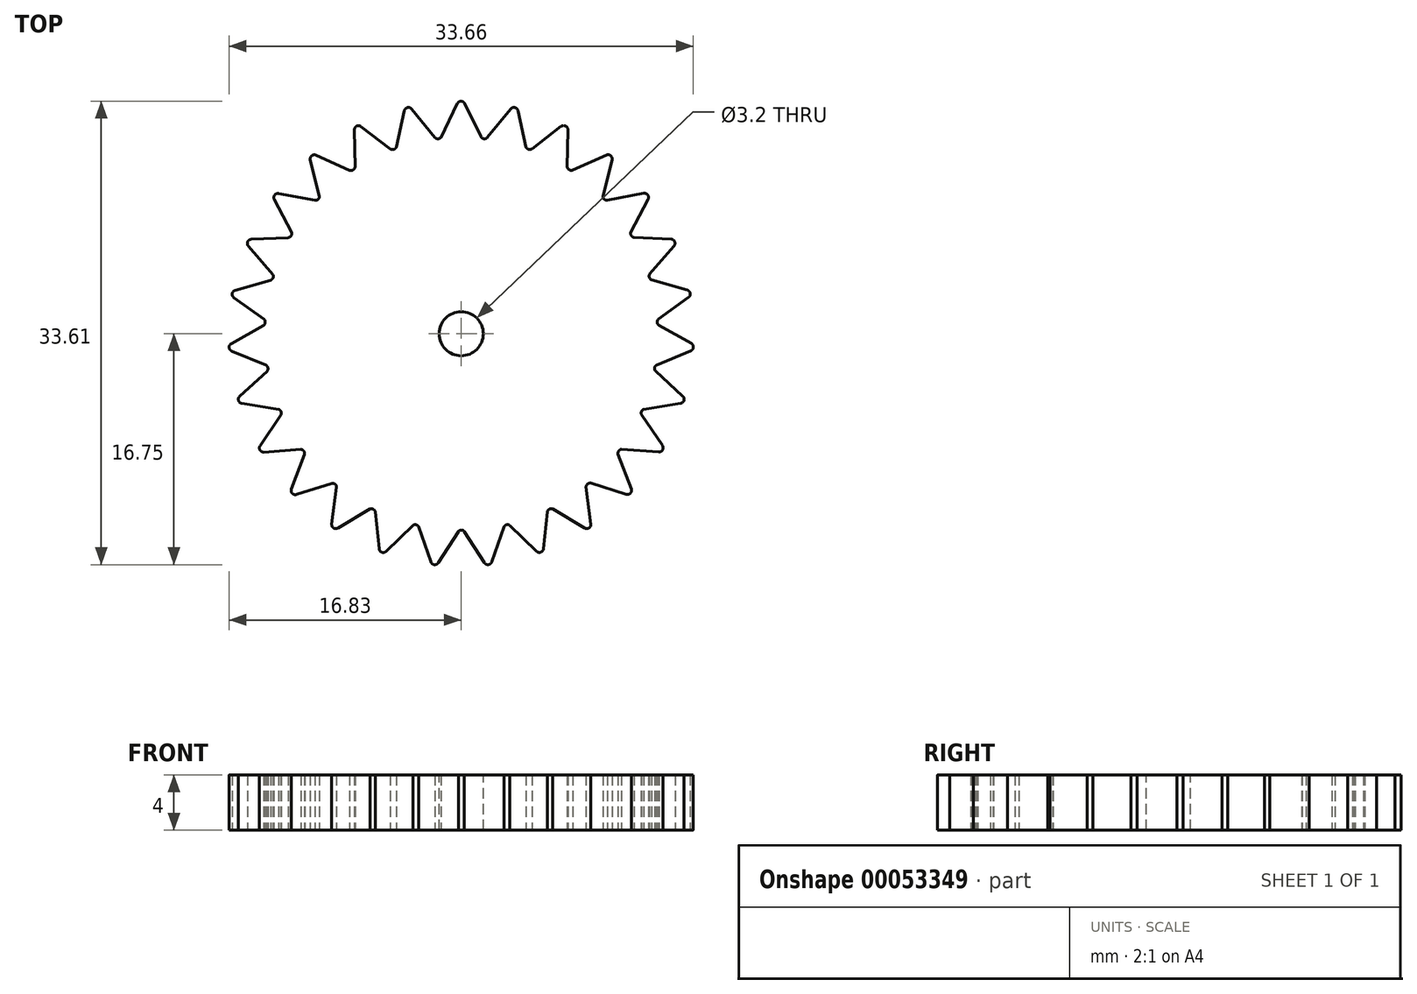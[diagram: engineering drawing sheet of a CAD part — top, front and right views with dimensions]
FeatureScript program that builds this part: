
annotation { "Feature Type Name" : "Feature", "Feature Type Description" : "" }
export const myFeature = defineFeature(function(context is Context, id is Id, definition is map)
    precondition{}
    {
        {
            var Q0;
            Q0=qCreatedBy(makeId("Top.planeOp"),FACE);
            var sketch = newSketch(context, id + "F0", { "sketchPlane" : qUnion([Q0])});
            skCircle(sketch, "E0", {"center": v(0, 0) * mm, "radius": 17.25 * mm, "construction": true});
            skCircle(sketch, "E1", {"center": v(0, 0) * mm, "radius": 14.25 * mm, "construction": true});
            skCircle(sketch, "E2", {"center": v(0, 0) * mm, "radius": 15.75 * mm, "construction": true});
            skLineSegment(sketch, "E3", {"start": v(-1.49, 14.17) * mm, "end": v(-0.27, 16.7) * mm});
            skLineSegment(sketch, "E4", {"start": v(1.49, 14.17) * mm, "end": v(0.27, 16.7) * mm});
            skPoint(sketch, "E5.visualSharp", {"position": v(0, 17.25) * mm});
            skArc(sketch, "E5.filletArc", {"start": v(0.27, 16.7) * mm, "mid": v(0, 16.86) * mm, "end": v(-0.27, 16.7) * mm});
            skLineSegment(sketch, "E6.1.0", {"start": v(4.72, 13.45) * mm, "end": v(4.11, 16.18) * mm});
            skLineSegment(sketch, "E6.1.1", {"start": v(1.91, 14.25) * mm, "end": v(3.59, 16.3) * mm});
            skArc(sketch, "E6.1.2", {"start": v(4.11, 16.18) * mm, "mid": v(3.89, 16.4) * mm, "end": v(3.59, 16.3) * mm});
            skLineSegment(sketch, "E6.2.0", {"start": v(7.7, 12) * mm, "end": v(7.73, 14.8) * mm});
            skLineSegment(sketch, "E6.2.1", {"start": v(5.03, 13.33) * mm, "end": v(7.25, 15.04) * mm});
            skArc(sketch, "E6.2.2", {"start": v(7.73, 14.8) * mm, "mid": v(7.57, 15.07) * mm, "end": v(7.25, 15.04) * mm});
            skLineSegment(sketch, "E6.3.0", {"start": v(10.25, 9.9) * mm, "end": v(10.94, 12.61) * mm});
            skLineSegment(sketch, "E6.3.1", {"start": v(7.97, 11.81) * mm, "end": v(10.52, 12.96) * mm});
            skArc(sketch, "E6.3.2", {"start": v(10.94, 12.61) * mm, "mid": v(10.84, 12.92) * mm, "end": v(10.52, 12.96) * mm});
            skLineSegment(sketch, "E6.4.0", {"start": v(12.26, 7.27) * mm, "end": v(13.55, 9.75) * mm});
            skLineSegment(sketch, "E6.4.1", {"start": v(10.48, 9.66) * mm, "end": v(13.23, 10.19) * mm});
            skArc(sketch, "E6.4.2", {"start": v(13.55, 9.75) * mm, "mid": v(13.52, 10.07) * mm, "end": v(13.23, 10.19) * mm});
            skLineSegment(sketch, "E6.5.0", {"start": v(13.6, 4.25) * mm, "end": v(15.43, 6.37) * mm});
            skLineSegment(sketch, "E6.5.1", {"start": v(12.42, 6.98) * mm, "end": v(15.22, 6.86) * mm});
            skArc(sketch, "E6.5.2", {"start": v(15.43, 6.37) * mm, "mid": v(15.48, 6.68) * mm, "end": v(15.22, 6.86) * mm});
            skLineSegment(sketch, "E6.6.0", {"start": v(14.22, 1) * mm, "end": v(16.48, 2.64) * mm});
            skLineSegment(sketch, "E6.6.1", {"start": v(13.7, 3.93) * mm, "end": v(16.4, 3.17) * mm});
            skArc(sketch, "E6.6.2", {"start": v(16.48, 2.64) * mm, "mid": v(16.6, 2.93) * mm, "end": v(16.4, 3.17) * mm});
            skLineSegment(sketch, "E6.7.0", {"start": v(14.06, -2.3) * mm, "end": v(16.65, -1.24) * mm});
            skLineSegment(sketch, "E6.7.1", {"start": v(14.23, 0.67) * mm, "end": v(16.68, -0.7) * mm});
            skArc(sketch, "E6.7.2", {"start": v(16.65, -1.24) * mm, "mid": v(16.83, -0.98) * mm, "end": v(16.68, -0.7) * mm});
            skLineSegment(sketch, "E6.8.0", {"start": v(13.15, -5.49) * mm, "end": v(15.91, -5.04) * mm});
            skLineSegment(sketch, "E6.8.1", {"start": v(14, -2.63) * mm, "end": v(16.07, -4.52) * mm});
            skArc(sketch, "E6.8.2", {"start": v(15.91, -5.04) * mm, "mid": v(16.15, -4.83) * mm, "end": v(16.07, -4.52) * mm});
            skLineSegment(sketch, "E6.9.0", {"start": v(11.53, -8.37) * mm, "end": v(14.32, -8.58) * mm});
            skLineSegment(sketch, "E6.9.1", {"start": v(13.02, -5.8) * mm, "end": v(14.6, -8.1) * mm});
            skArc(sketch, "E6.9.2", {"start": v(14.32, -8.58) * mm, "mid": v(14.6, -8.43) * mm, "end": v(14.6, -8.1) * mm});
            skLineSegment(sketch, "E7.1.10.0", {"start": v(9.29, -10.8) * mm, "end": v(11.96, -11.65) * mm});
            skLineSegment(sketch, "E7.3.10.0", {"start": v(11.33, -8.64) * mm, "end": v(12.33, -11.25) * mm});
            skArc(sketch, "E7.6.10.0", {"start": v(11.96, -11.65) * mm, "mid": v(12.27, -11.57) * mm, "end": v(12.33, -11.25) * mm});
            skLineSegment(sketch, "E7.1.11.0", {"start": v(6.55, -12.66) * mm, "end": v(8.95, -14.1) * mm});
            skLineSegment(sketch, "E7.3.11.0", {"start": v(9.04, -11.02) * mm, "end": v(9.4, -13.8) * mm});
            skArc(sketch, "E7.6.11.0", {"start": v(8.95, -14.1) * mm, "mid": v(9.27, -14.08) * mm, "end": v(9.4, -13.8) * mm});
            skLineSegment(sketch, "E7.1.12.0", {"start": v(3.45, -13.83) * mm, "end": v(5.46, -15.78) * mm});
            skLineSegment(sketch, "E7.3.12.0", {"start": v(6.25, -12.8) * mm, "end": v(5.97, -15.6) * mm});
            skArc(sketch, "E7.6.12.0", {"start": v(5.46, -15.78) * mm, "mid": v(5.77, -15.84) * mm, "end": v(5.97, -15.6) * mm});
            skLineSegment(sketch, "E7.1.13.0", {"start": v(0.17, -14.25) * mm, "end": v(1.68, -16.6) * mm});
            skLineSegment(sketch, "E7.3.13.0", {"start": v(3.13, -13.9) * mm, "end": v(2.21, -16.55) * mm});
            skArc(sketch, "E7.6.13.0", {"start": v(1.68, -16.6) * mm, "mid": v(1.96, -16.75) * mm, "end": v(2.21, -16.55) * mm});
            skLineSegment(sketch, "E7.1.14.0", {"start": v(-3.12, -13.9) * mm, "end": v(-2.2, -16.55) * mm});
            skLineSegment(sketch, "E7.3.14.0", {"start": v(-0.16, -14.25) * mm, "end": v(-1.66, -16.61) * mm});
            skArc(sketch, "E7.6.14.0", {"start": v(-2.2, -16.55) * mm, "mid": v(-1.95, -16.75) * mm, "end": v(-1.66, -16.61) * mm});
            skLineSegment(sketch, "E7.1.15.0", {"start": v(-6.24, -12.81) * mm, "end": v(-5.96, -15.6) * mm});
            skLineSegment(sketch, "E7.3.15.0", {"start": v(-3.44, -13.83) * mm, "end": v(-5.45, -15.78) * mm});
            skArc(sketch, "E7.6.15.0", {"start": v(-5.96, -15.6) * mm, "mid": v(-5.76, -15.85) * mm, "end": v(-5.45, -15.78) * mm});
            skLineSegment(sketch, "E7.1.16.0", {"start": v(-9.03, -11.03) * mm, "end": v(-9.4, -13.8) * mm});
            skLineSegment(sketch, "E7.3.16.0", {"start": v(-6.54, -12.66) * mm, "end": v(-8.94, -14.1) * mm});
            skArc(sketch, "E7.6.16.0", {"start": v(-9.4, -13.8) * mm, "mid": v(-9.26, -14.1) * mm, "end": v(-8.94, -14.1) * mm});
            skLineSegment(sketch, "E7.1.17.0", {"start": v(-11.33, -8.65) * mm, "end": v(-12.32, -11.26) * mm});
            skLineSegment(sketch, "E7.3.17.0", {"start": v(-9.28, -10.81) * mm, "end": v(-11.95, -11.66) * mm});
            skArc(sketch, "E7.6.17.0", {"start": v(-12.32, -11.26) * mm, "mid": v(-12.26, -11.58) * mm, "end": v(-11.95, -11.66) * mm});
            skLineSegment(sketch, "E7.1.18.0", {"start": v(-13.01, -5.8) * mm, "end": v(-14.59, -8.12) * mm});
            skLineSegment(sketch, "E7.3.18.0", {"start": v(-11.52, -8.38) * mm, "end": v(-14.32, -8.59) * mm});
            skArc(sketch, "E7.6.18.0", {"start": v(-14.59, -8.12) * mm, "mid": v(-14.6, -8.44) * mm, "end": v(-14.32, -8.59) * mm});
            skLineSegment(sketch, "E7.1.19.0", {"start": v(-14, -2.65) * mm, "end": v(-16.07, -4.54) * mm});
            skLineSegment(sketch, "E7.3.19.0", {"start": v(-13.15, -5.5) * mm, "end": v(-15.91, -5.06) * mm});
            skArc(sketch, "E7.6.19.0", {"start": v(-16.07, -4.54) * mm, "mid": v(-16.15, -4.85) * mm, "end": v(-15.91, -5.06) * mm});
            skLineSegment(sketch, "E8", {"start": v(1.49, 14.17) * mm, "end": v(0, 0) * mm, "construction": true});
            skLineSegment(sketch, "E9", {"start": v(-1.49, 14.17) * mm, "end": v(0, 0) * mm, "construction": true});
            skLineSegment(sketch, "E10.1.20.0", {"start": v(-14.23, 0.65) * mm, "end": v(-16.68, -0.71) * mm});
            skLineSegment(sketch, "E10.3.20.0", {"start": v(-14.06, -2.32) * mm, "end": v(-16.65, -1.25) * mm});
            skArc(sketch, "E10.6.20.0", {"start": v(-16.68, -0.71) * mm, "mid": v(-16.83, -1) * mm, "end": v(-16.65, -1.25) * mm});
            skLineSegment(sketch, "E10.1.21.0", {"start": v(-13.7, 3.92) * mm, "end": v(-16.4, 3.15) * mm});
            skLineSegment(sketch, "E10.3.21.0", {"start": v(-14.22, 0.98) * mm, "end": v(-16.49, 2.62) * mm});
            skArc(sketch, "E10.6.21.0", {"start": v(-16.4, 3.15) * mm, "mid": v(-16.6, 2.92) * mm, "end": v(-16.49, 2.62) * mm});
            skLineSegment(sketch, "E10.1.22.0", {"start": v(-12.43, 6.97) * mm, "end": v(-15.22, 6.85) * mm});
            skLineSegment(sketch, "E10.3.22.0", {"start": v(-13.6, 4.24) * mm, "end": v(-15.44, 6.35) * mm});
            skArc(sketch, "E10.6.22.0", {"start": v(-15.22, 6.85) * mm, "mid": v(-15.49, 6.67) * mm, "end": v(-15.44, 6.35) * mm});
            skLineSegment(sketch, "E10.1.23.0", {"start": v(-10.49, 9.65) * mm, "end": v(-13.24, 10.17) * mm});
            skLineSegment(sketch, "E10.3.23.0", {"start": v(-12.26, 7.26) * mm, "end": v(-13.56, 9.74) * mm});
            skArc(sketch, "E10.6.23.0", {"start": v(-13.24, 10.17) * mm, "mid": v(-13.53, 10.06) * mm, "end": v(-13.56, 9.74) * mm});
            skLineSegment(sketch, "E10.1.24.0", {"start": v(-7.98, 11.8) * mm, "end": v(-10.53, 12.95) * mm});
            skLineSegment(sketch, "E10.3.24.0", {"start": v(-10.26, 9.9) * mm, "end": v(-10.95, 12.6) * mm});
            skArc(sketch, "E10.6.24.0", {"start": v(-10.53, 12.95) * mm, "mid": v(-10.85, 12.9) * mm, "end": v(-10.95, 12.6) * mm});
            skLineSegment(sketch, "E10.1.25.0", {"start": v(-5.04, 13.33) * mm, "end": v(-7.26, 15.03) * mm});
            skLineSegment(sketch, "E10.3.25.0", {"start": v(-7.7, 11.99) * mm, "end": v(-7.74, 14.79) * mm});
            skArc(sketch, "E10.6.25.0", {"start": v(-7.26, 15.03) * mm, "mid": v(-7.58, 15.06) * mm, "end": v(-7.74, 14.79) * mm});
            skPoint(sketch, "E11.newPointB", {"position": v(1.82, 14.13) * mm});
            skArc(sketch, "E11.filletArc", {"start": v(1.41, 14.31) * mm, "mid": v(1.65, 14.14) * mm, "end": v(1.91, 14.25) * mm});
            skArc(sketch, "E12.1.0", {"start": v(-1.93, 14.25) * mm, "mid": v(-1.66, 14.14) * mm, "end": v(-1.42, 14.3) * mm});
            skArc(sketch, "E12.2.0", {"start": v(-5.16, 13.42) * mm, "mid": v(-4.88, 13.38) * mm, "end": v(-4.69, 13.6) * mm});
            skArc(sketch, "E12.3.0", {"start": v(-8.12, 11.87) * mm, "mid": v(-7.83, 11.9) * mm, "end": v(-7.7, 12.15) * mm});
            skArc(sketch, "E12.4.0", {"start": v(-10.64, 9.68) * mm, "mid": v(-10.36, 9.77) * mm, "end": v(-10.29, 10.05) * mm});
            skArc(sketch, "E12.5.0", {"start": v(-12.58, 6.96) * mm, "mid": v(-12.33, 7.11) * mm, "end": v(-12.33, 7.4) * mm});
            skArc(sketch, "E12.6.0", {"start": v(-13.85, 3.87) * mm, "mid": v(-13.64, 4.08) * mm, "end": v(-13.7, 4.36) * mm});
            skArc(sketch, "E12.7.0", {"start": v(-14.37, 0.58) * mm, "mid": v(-14.21, 0.82) * mm, "end": v(-14.34, 1.08) * mm});
            skArc(sketch, "E12.8.0", {"start": v(-14.11, -2.75) * mm, "mid": v(-14.02, -2.48) * mm, "end": v(-14.2, -2.25) * mm});
            skArc(sketch, "E12.9.0", {"start": v(-13.1, -5.93) * mm, "mid": v(-13.07, -5.65) * mm, "end": v(-13.3, -5.47) * mm});
            skArc(sketch, "E12.10.0", {"start": v(-11.38, -8.8) * mm, "mid": v(-11.42, -8.5) * mm, "end": v(-11.68, -8.39) * mm});
            skArc(sketch, "E12.11.0", {"start": v(-9.04, -11.18) * mm, "mid": v(-9.15, -10.91) * mm, "end": v(-9.43, -10.85) * mm});
            skArc(sketch, "E12.12.0", {"start": v(-6.22, -12.96) * mm, "mid": v(-6.38, -12.73) * mm, "end": v(-6.67, -12.74) * mm});
            skArc(sketch, "E12.13.0", {"start": v(-3.06, -14.05) * mm, "mid": v(-3.28, -13.86) * mm, "end": v(-3.56, -13.93) * mm});
            skArc(sketch, "E12.14.0", {"start": v(0.26, -14.38) * mm, "mid": v(0, -14.24) * mm, "end": v(-0.25, -14.38) * mm});
            skArc(sketch, "E12.15.0", {"start": v(3.57, -13.93) * mm, "mid": v(3.3, -13.85) * mm, "end": v(3.08, -14.05) * mm});
            skArc(sketch, "E12.16.0", {"start": v(6.68, -12.73) * mm, "mid": v(6.4, -12.72) * mm, "end": v(6.23, -12.96) * mm});
            skArc(sketch, "E12.17.0", {"start": v(9.44, -10.85) * mm, "mid": v(9.16, -10.9) * mm, "end": v(9.05, -11.17) * mm});
            skArc(sketch, "E12.18.0", {"start": v(11.69, -8.38) * mm, "mid": v(11.42, -8.5) * mm, "end": v(11.38, -8.78) * mm});
            skArc(sketch, "E12.19.0", {"start": v(13.3, -5.46) * mm, "mid": v(13.08, -5.63) * mm, "end": v(13.1, -5.92) * mm});
            skArc(sketch, "E12.20.0", {"start": v(14.2, -2.24) * mm, "mid": v(14.02, -2.47) * mm, "end": v(14.12, -2.74) * mm});
            skArc(sketch, "E12.21.0", {"start": v(14.34, 1.1) * mm, "mid": v(14.21, 0.83) * mm, "end": v(14.37, 0.59) * mm});
            skArc(sketch, "E12.22.0", {"start": v(13.7, 4.37) * mm, "mid": v(13.64, 4.09) * mm, "end": v(13.84, 3.89) * mm});
            skArc(sketch, "E12.23.0", {"start": v(12.32, 7.41) * mm, "mid": v(12.33, 7.12) * mm, "end": v(12.57, 6.97) * mm});
            skArc(sketch, "E12.24.0", {"start": v(10.28, 10.06) * mm, "mid": v(10.35, 9.78) * mm, "end": v(10.63, 9.69) * mm});
            skLineSegment(sketch, "E13.1.26.0", {"start": v(-1.83, 14.13) * mm, "end": v(-3.6, 16.3) * mm});
            skLineSegment(sketch, "E13.3.26.0", {"start": v(-4.73, 13.44) * mm, "end": v(-4.13, 16.18) * mm});
            skArc(sketch, "E13.6.26.0", {"start": v(-3.6, 16.3) * mm, "mid": v(-3.9, 16.4) * mm, "end": v(-4.13, 16.18) * mm});
            skLineSegment(sketch, "E14.1.27.0", {"start": v(1.48, 14.17) * mm, "end": v(0.26, 16.7) * mm});
            skLineSegment(sketch, "E14.3.27.0", {"start": v(-1.5, 14.17) * mm, "end": v(-0.28, 16.7) * mm});
            skArc(sketch, "E14.6.27.0", {"start": v(0.26, 16.7) * mm, "mid": v(-0.01, 16.86) * mm, "end": v(-0.28, 16.7) * mm});
            skArc(sketch, "E15.2.25.0", {"start": v(7.68, 12.15) * mm, "mid": v(7.82, 11.9) * mm, "end": v(8.1, 11.88) * mm});
            skArc(sketch, "E15.2.26.0", {"start": v(4.67, 13.6) * mm, "mid": v(4.86, 13.38) * mm, "end": v(5.15, 13.43) * mm});
            skSolve(sketch);
        }
        {
            var Q0;
            Q0=makeQuery(id+"F0.imprint","IMPRINT",FACE,{"disambiguationData":[TD([[makeQuery(id+"F0.imprint","IMPRINT",EDGE,{"derivedFrom":sQuery(id+"F0.wireOp",EDGE,"E6.1.1")}),-1.0]])]});
            extrude(context, id + "F1", {"entities" : qUnion([Q0]), "depth" : 4 * mm});
        }
        {
            var Q0;
            Q0=makeQuery(id+"F1.opExtrude","CAP_FACE",FACE,{"disambiguationData":[OSD([sQuery(id+"F0.wireOp",EDGE,"E6.1.0"),sQuery(id+"F0.wireOp",EDGE,"E6.1.1"),sQuery(id+"F0.wireOp",EDGE,"E6.1.2"),sQuery(id+"F0.wireOp",EDGE,"E6.2.0"),sQuery(id+"F0.wireOp",EDGE,"E6.2.1"),sQuery(id+"F0.wireOp",EDGE,"E6.2.2"),sQuery(id+"F0.wireOp",EDGE,"E6.3.0"),sQuery(id+"F0.wireOp",EDGE,"E6.3.1"),sQuery(id+"F0.wireOp",EDGE,"E6.3.2"),sQuery(id+"F0.wireOp",EDGE,"E6.4.0"),sQuery(id+"F0.wireOp",EDGE,"E6.4.1"),sQuery(id+"F0.wireOp",EDGE,"E6.4.2"),sQuery(id+"F0.wireOp",EDGE,"E6.5.0"),sQuery(id+"F0.wireOp",EDGE,"E6.5.1"),sQuery(id+"F0.wireOp",EDGE,"E6.5.2"),sQuery(id+"F0.wireOp",EDGE,"E6.6.0"),sQuery(id+"F0.wireOp",EDGE,"E6.6.1"),sQuery(id+"F0.wireOp",EDGE,"E6.6.2"),sQuery(id+"F0.wireOp",EDGE,"E6.7.0"),sQuery(id+"F0.wireOp",EDGE,"E6.7.1"),sQuery(id+"F0.wireOp",EDGE,"E6.7.2"),sQuery(id+"F0.wireOp",EDGE,"E6.8.0"),sQuery(id+"F0.wireOp",EDGE,"E6.8.1"),sQuery(id+"F0.wireOp",EDGE,"E6.8.2"),sQuery(id+"F0.wireOp",EDGE,"E6.9.0"),sQuery(id+"F0.wireOp",EDGE,"E6.9.1"),sQuery(id+"F0.wireOp",EDGE,"E6.9.2"),sQuery(id+"F0.wireOp",EDGE,"E7.1.10.0"),sQuery(id+"F0.wireOp",EDGE,"E7.3.10.0"),sQuery(id+"F0.wireOp",EDGE,"E7.6.10.0"),sQuery(id+"F0.wireOp",EDGE,"E7.1.11.0"),sQuery(id+"F0.wireOp",EDGE,"E7.3.11.0"),sQuery(id+"F0.wireOp",EDGE,"E7.6.11.0"),sQuery(id+"F0.wireOp",EDGE,"E7.1.12.0"),sQuery(id+"F0.wireOp",EDGE,"E7.3.12.0"),sQuery(id+"F0.wireOp",EDGE,"E7.6.12.0"),sQuery(id+"F0.wireOp",EDGE,"E7.1.13.0"),sQuery(id+"F0.wireOp",EDGE,"E7.3.13.0"),sQuery(id+"F0.wireOp",EDGE,"E7.6.13.0"),sQuery(id+"F0.wireOp",EDGE,"E7.1.14.0"),sQuery(id+"F0.wireOp",EDGE,"E7.3.14.0"),sQuery(id+"F0.wireOp",EDGE,"E7.6.14.0"),sQuery(id+"F0.wireOp",EDGE,"E7.1.15.0"),sQuery(id+"F0.wireOp",EDGE,"E7.3.15.0"),sQuery(id+"F0.wireOp",EDGE,"E7.6.15.0"),sQuery(id+"F0.wireOp",EDGE,"E7.1.16.0"),sQuery(id+"F0.wireOp",EDGE,"E7.3.16.0"),sQuery(id+"F0.wireOp",EDGE,"E7.6.16.0"),sQuery(id+"F0.wireOp",EDGE,"E7.1.17.0"),sQuery(id+"F0.wireOp",EDGE,"E7.3.17.0"),sQuery(id+"F0.wireOp",EDGE,"E7.6.17.0"),sQuery(id+"F0.wireOp",EDGE,"E7.1.18.0"),sQuery(id+"F0.wireOp",EDGE,"E7.3.18.0"),sQuery(id+"F0.wireOp",EDGE,"E7.6.18.0"),sQuery(id+"F0.wireOp",EDGE,"E7.1.19.0"),sQuery(id+"F0.wireOp",EDGE,"E7.3.19.0"),sQuery(id+"F0.wireOp",EDGE,"E7.6.19.0"),sQuery(id+"F0.wireOp",EDGE,"E10.1.20.0"),sQuery(id+"F0.wireOp",EDGE,"E10.3.20.0"),sQuery(id+"F0.wireOp",EDGE,"E10.6.20.0"),sQuery(id+"F0.wireOp",EDGE,"E10.1.21.0"),sQuery(id+"F0.wireOp",EDGE,"E10.3.21.0"),sQuery(id+"F0.wireOp",EDGE,"E10.6.21.0"),sQuery(id+"F0.wireOp",EDGE,"E10.1.22.0"),sQuery(id+"F0.wireOp",EDGE,"E10.3.22.0"),sQuery(id+"F0.wireOp",EDGE,"E10.6.22.0"),sQuery(id+"F0.wireOp",EDGE,"E10.1.23.0"),sQuery(id+"F0.wireOp",EDGE,"E10.3.23.0"),sQuery(id+"F0.wireOp",EDGE,"E10.6.23.0"),sQuery(id+"F0.wireOp",EDGE,"E10.1.24.0"),sQuery(id+"F0.wireOp",EDGE,"E10.3.24.0"),sQuery(id+"F0.wireOp",EDGE,"E10.6.24.0"),sQuery(id+"F0.wireOp",EDGE,"E10.1.25.0"),sQuery(id+"F0.wireOp",EDGE,"E10.3.25.0"),sQuery(id+"F0.wireOp",EDGE,"E10.6.25.0"),sQuery(id+"F0.wireOp",EDGE,"E10.1.26.0"),sQuery(id+"F0.wireOp",EDGE,"E10.3.26.0"),sQuery(id+"F0.wireOp",EDGE,"E10.6.26.0"),sQuery(id+"F0.wireOp",EDGE,"E10.1.27.0"),sQuery(id+"F0.wireOp",EDGE,"E10.3.27.0"),sQuery(id+"F0.wireOp",EDGE,"E10.6.27.0"),sQuery(id+"F0.wireOp",EDGE,"E10.1.28.0"),sQuery(id+"F0.wireOp",EDGE,"E10.3.28.0"),sQuery(id+"F0.wireOp",EDGE,"E10.6.28.0"),sQuery(id+"F0.wireOp",EDGE,"E10.1.29.0"),sQuery(id+"F0.wireOp",EDGE,"E10.3.29.0"),sQuery(id+"F0.wireOp",EDGE,"E10.6.29.0"),sQuery(id+"F0.wireOp",EDGE,"E11.filletArc"),sQuery(id+"F0.wireOp",EDGE,"E12.1.0"),sQuery(id+"F0.wireOp",EDGE,"E12.2.0"),sQuery(id+"F0.wireOp",EDGE,"E12.3.0"),sQuery(id+"F0.wireOp",EDGE,"E12.4.0"),sQuery(id+"F0.wireOp",EDGE,"E12.5.0"),sQuery(id+"F0.wireOp",EDGE,"E12.6.0"),sQuery(id+"F0.wireOp",EDGE,"E12.7.0"),sQuery(id+"F0.wireOp",EDGE,"E12.8.0"),sQuery(id+"F0.wireOp",EDGE,"E12.9.0"),sQuery(id+"F0.wireOp",EDGE,"E12.10.0"),sQuery(id+"F0.wireOp",EDGE,"E12.11.0"),sQuery(id+"F0.wireOp",EDGE,"E12.12.0"),sQuery(id+"F0.wireOp",EDGE,"E12.13.0"),sQuery(id+"F0.wireOp",EDGE,"E12.14.0"),sQuery(id+"F0.wireOp",EDGE,"E12.15.0"),sQuery(id+"F0.wireOp",EDGE,"E12.16.0"),sQuery(id+"F0.wireOp",EDGE,"E12.17.0"),sQuery(id+"F0.wireOp",EDGE,"E12.18.0"),sQuery(id+"F0.wireOp",EDGE,"E12.19.0"),sQuery(id+"F0.wireOp",EDGE,"E12.20.0"),sQuery(id+"F0.wireOp",EDGE,"E12.21.0"),sQuery(id+"F0.wireOp",EDGE,"E12.22.0"),sQuery(id+"F0.wireOp",EDGE,"E12.23.0"),sQuery(id+"F0.wireOp",EDGE,"E12.24.0"),sQuery(id+"F0.wireOp",EDGE,"E12.25.0"),sQuery(id+"F0.wireOp",EDGE,"E12.26.0"),sQuery(id+"F0.wireOp",EDGE,"E12.27.0"),sQuery(id+"F0.wireOp",EDGE,"E12.28.0")])],"isStart":false});
            var sketch = newSketch(context, id + "F2", { "sketchPlane" : qUnion([Q0])});
            skCircle(sketch, "E16", {"center": v(0, 0) * mm, "radius": 1.6 * mm});
            skSolve(sketch);
        }
        {
            var Q0;
            Q0 = qSketchRegion(id + "F2", true);
            extrude(context, id + "F3", {"entities" : qUnion([Q0]), "operationType" : NewBodyOperationType.REMOVE, "endBound" : BoundingType.THROUGH_ALL, "oppositeDirection" : true, "depth" : 25 * mm});
        }
    });
